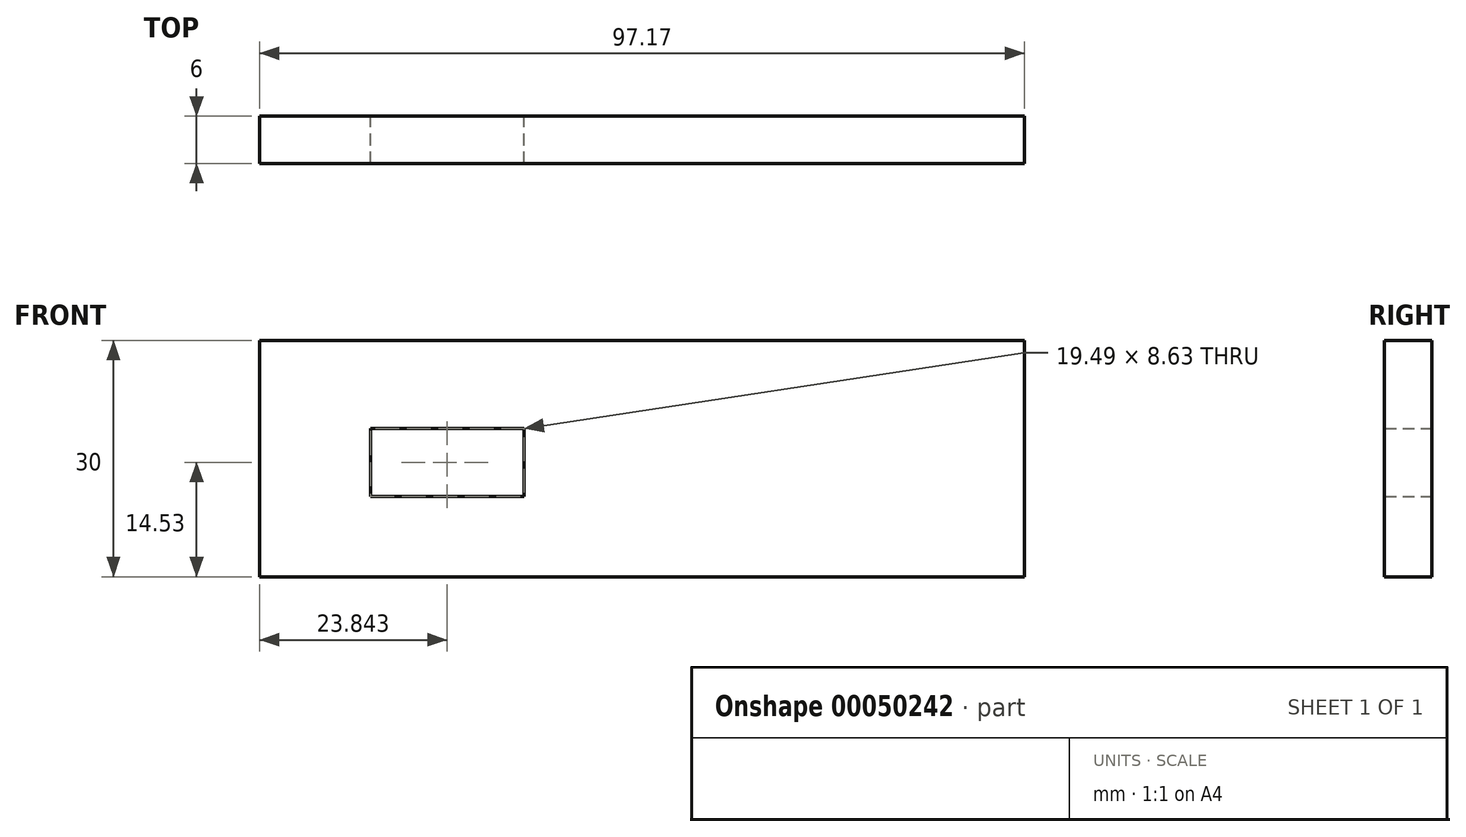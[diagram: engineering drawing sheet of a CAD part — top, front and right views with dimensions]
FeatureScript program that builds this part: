
annotation { "Feature Type Name" : "Feature", "Feature Type Description" : "" }
export const myFeature = defineFeature(function(context is Context, id is Id, definition is map)
    precondition{}
    {
        {
            var Q0;
            Q0=qCreatedBy(makeId("Front.planeOp"),FACE);
            var sketch = newSketch(context, id + "F0", { "sketchPlane" : qUnion([Q0])});
            skLineSegment(sketch, "E0.bottom", {"start": v(0, 0) * mm, "end": v(97.17, 0) * mm});
            skLineSegment(sketch, "E0.top", {"start": v(0, 30) * mm, "end": v(97.17, 30) * mm});
            skLineSegment(sketch, "E0.left", {"start": v(0, 0) * mm, "end": v(0, 30) * mm});
            skLineSegment(sketch, "E0.right", {"start": v(97.17, 0) * mm, "end": v(97.17, 30) * mm});
            skLineSegment(sketch, "E1.bottom", {"start": v(14.1, 10.22) * mm, "end": v(33.59, 10.22) * mm});
            skLineSegment(sketch, "E1.top", {"start": v(14.1, 18.84) * mm, "end": v(33.59, 18.84) * mm});
            skLineSegment(sketch, "E1.left", {"start": v(14.1, 10.22) * mm, "end": v(14.1, 18.84) * mm});
            skLineSegment(sketch, "E1.right", {"start": v(33.59, 10.22) * mm, "end": v(33.59, 18.84) * mm});
            skSolve(sketch);
        }
        {
            var Q0;
            Q0 = qSketchRegion(id + "F0", true);
            extrude(context, id + "F1", {"entities" : qUnion([Q0]), "depth" : 6 * mm});
        }
    });
